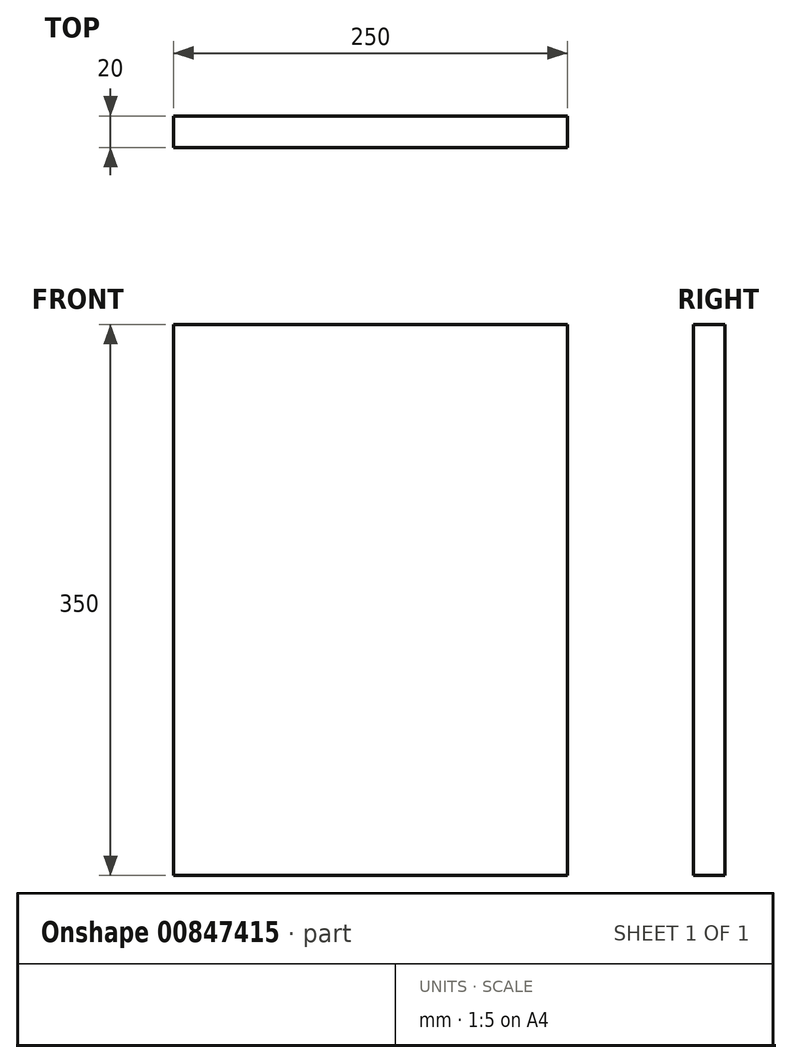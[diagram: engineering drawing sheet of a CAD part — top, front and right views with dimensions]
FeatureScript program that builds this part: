
annotation { "Feature Type Name" : "Feature", "Feature Type Description" : "" }
export const myFeature = defineFeature(function(context is Context, id is Id, definition is map)
    precondition{}
    {
        {
            var Q0;
            Q0=qCreatedBy(makeId("Front.planeOp"),FACE);
            var sketch = newSketch(context, id + "F0", { "sketchPlane" : qUnion([Q0])});
            skLineSegment(sketch, "E0.bottom", {"start": v(-125, 175) * mm, "end": v(125, 175) * mm});
            skLineSegment(sketch, "E0.top", {"start": v(-125, -175) * mm, "end": v(125, -175) * mm});
            skLineSegment(sketch, "E0.left", {"start": v(-125, 175) * mm, "end": v(-125, -175) * mm});
            skLineSegment(sketch, "E0.right", {"start": v(125, 175) * mm, "end": v(125, -175) * mm});
            skPoint(sketch, "E0.middle", {"position": v(0, 0) * mm});
            skSolve(sketch);
        }
        {
            var Q0;
            Q0 = qSketchRegion(id + "F0", true);
            extrude(context, id + "F1", {"entities" : qUnion([Q0]), "endBound" : BoundingType.SYMMETRIC, "depth" : 20 * mm, "offsetDistance" : 25 * mm});
        }
    });
